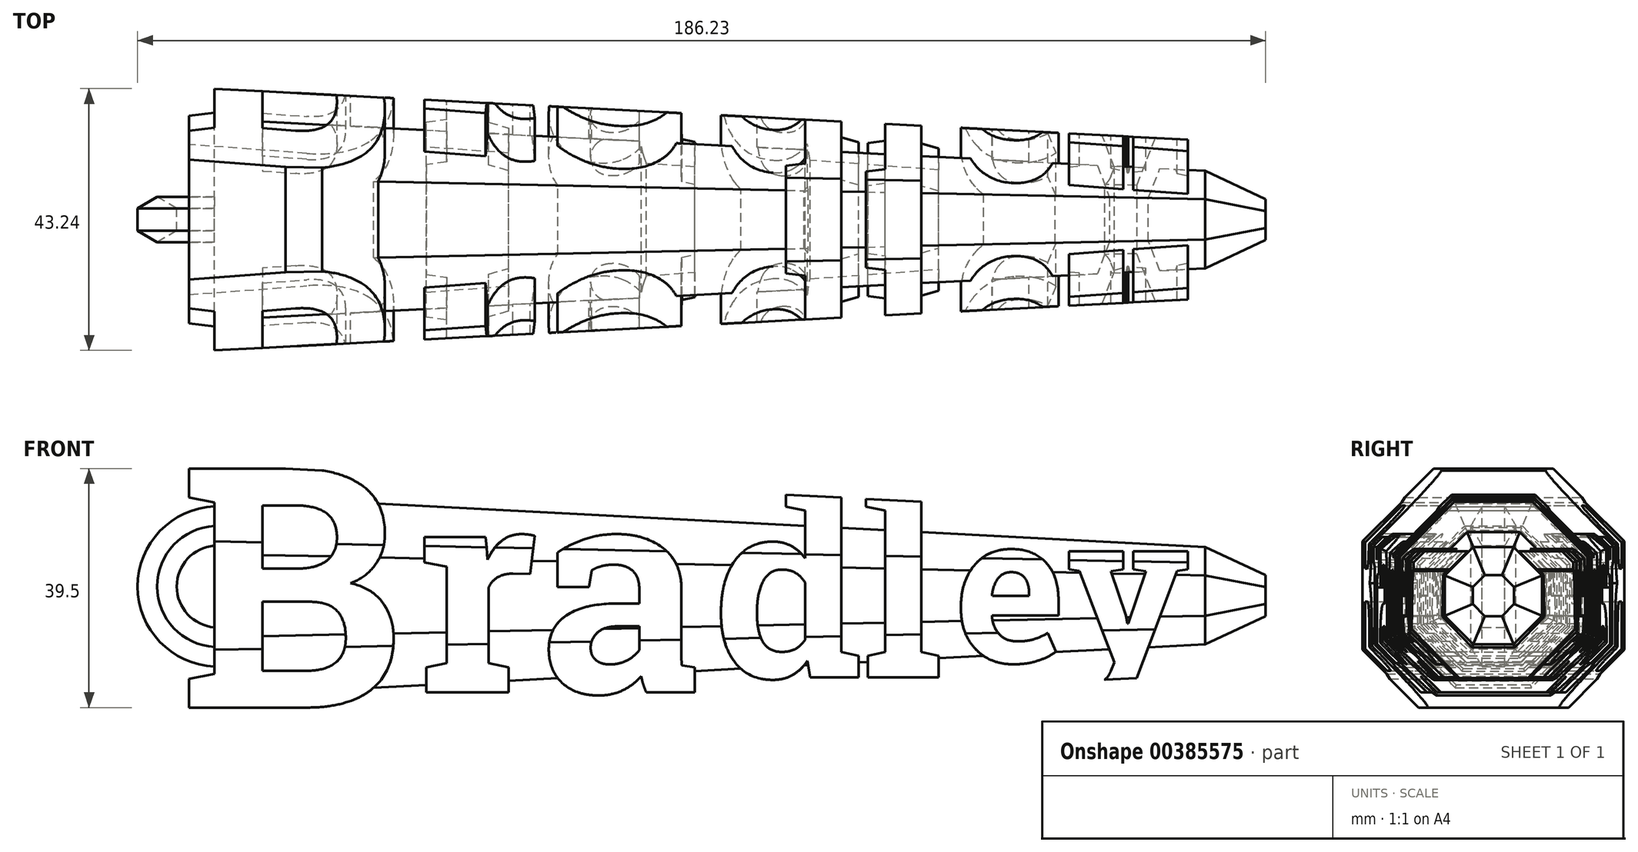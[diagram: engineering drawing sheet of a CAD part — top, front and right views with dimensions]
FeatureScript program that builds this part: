
annotation { "Feature Type Name" : "Feature", "Feature Type Description" : "" }
export const myFeature = defineFeature(function(context is Context, id is Id, definition is map)
    precondition{}
    {
        {
            assignVariable(context, id + "F0", {"name" : "hookPlane", "anyValue" : 78});
        }
        {
            var Q0;
            Q0=qCreatedBy(makeId("Front.planeOp"),FACE);
            var sketch = newSketch(context, id + "F1", { "sketchPlane" : qUnion([Q0])});
            skText(sketch, "E0", { "text": "B", "fontName": "RobotoSlab-Bold.ttf"});
            skPoint(sketch, "E1", {"position": v(-45.56, 0) * mm});
            skText(sketch, "E2", { "text": "ra", "fontName": "RobotoSlab-Bold.ttf"});
            skText(sketch, "E3", { "text": "dl", "fontName": "RobotoSlab-Bold.ttf"});
            skText(sketch, "E4", { "text": "ey", "fontName": "RobotoSlab-Bold.ttf"});
            skPoint(sketch, "E5", {"position": v(3.73, 0) * mm});
            skPoint(sketch, "E6", {"position": v(43.58, 0) * mm});
            skLineSegment(sketch, "E7", {"start": v(-84.26, -20) * mm, "end": v(-84.26, -51.65) * mm, "construction": true});
            skLineSegment(sketch, "E8", {"start": v(-84.26, -51.65) * mm, "end": v(84.26, -51.65) * mm, "construction": true});
            skLineSegment(sketch, "E9", {"start": v(84.26, -51.65) * mm, "end": v(84.26, -12.5) * mm, "construction": true});
            skPoint(sketch, "E10", {"position": v(0, -51.65) * mm});
            const initialGuessF1  = {"E0": [-0.08426, -0.02, 1, 0, 0.04], "E2": [-0.04556, -0.0175, 1, 0, 0.035], "E3": [0.00373, -0.015, 1, 0, 0.03], "E4": [0.04358, -0.0125, 1, 0, 0.025]};
            skSetInitialGuess(sketch, initialGuessF1);
            skSolve(sketch);
        }
        {
            var Q0;
            Q0=qSketchRegion(id+"F1",true);
            extrude(context, id + "F2", {"entities" : qUnion([Q0]), "depth" : 25 * mm, "hasSecondDirection" : true, "secondDirectionOppositeDirection" : true, "secondDirectionDepth" : 25 * mm});
        }
        {
            var Q0;
            Q0=qCreatedBy(makeId("Right.planeOp"),FACE);
            var sketch = newSketch(context, id + "F3", { "sketchPlane" : qUnion([Q0])});
            skCircle(sketch, "E11", {"center": v(0, -1.5) * mm, "radius": 12.5 * mm, "construction": true});
            skLineSegment(sketch, "E12", {"start": v(0, 19.5) * mm, "end": v(0, -20) * mm, "construction": true});
            skLineSegment(sketch, "E13.0", {"start": v(-5.18, 11) * mm, "end": v(5.18, 11) * mm});
            skLineSegment(sketch, "E13.1", {"start": v(5.18, 11) * mm, "end": v(12.5, 3.67) * mm});
            skLineSegment(sketch, "E13.2", {"start": v(12.5, 3.67) * mm, "end": v(12.5, -6.68) * mm});
            skLineSegment(sketch, "E13.3", {"start": v(12.5, -6.68) * mm, "end": v(5.18, -14) * mm});
            skLineSegment(sketch, "E13.4", {"start": v(5.18, -14) * mm, "end": v(-5.18, -14) * mm});
            skLineSegment(sketch, "E13.5", {"start": v(-5.18, -14) * mm, "end": v(-12.5, -6.68) * mm});
            skLineSegment(sketch, "E13.6", {"start": v(-12.5, -6.68) * mm, "end": v(-12.5, 3.67) * mm});
            skLineSegment(sketch, "E13.7", {"start": v(-12.5, 3.67) * mm, "end": v(-5.18, 11) * mm});
            skPoint(sketch, "E13.0.midPoint", {"position": v(0, 11) * mm});
            skSolve(sketch);
        }
        {
            var Q0;
            Q0=qSketchRegion(id+"F3",true);
            var Q1;
            Q1=makeQuery(id+"F2.opExtrude","SWEPT_FACE",FACE,{"disambiguationData":[OSD([sQuery(id+"F1.wireOp",EDGE,"E4.sketch_text.stroke-1")])]});
            extrude(context, id + "F4", {"entities" : qUnion([Q0]), "operationType" : NewBodyOperationType.ADD, "oppositeDirection" : true, "depth" : 78 * mm, "hasDraft" : true, "draftAngle" : 3 * degree, "hasSecondDirection" : true, "secondDirectionOppositeDirection" : false, "secondDirectionBoundEntityFace" : qUnion([Q1]), "secondDirectionDepth" : 85 * mm, "hasSecondDirectionDraft" : true, "secondDirectionDraftAngle" : 3 * degree, "secondDirectionDraftPullDirection" : true});
        }
        {
            var Q0;
            Q0=qCreatedBy(makeId("Right.planeOp"),FACE);
            var sketch = newSketch(context, id + "F5", { "sketchPlane" : qUnion([Q0])});
            skCircle(sketch, "E14.cCircle", {"center": v(0, -1.5) * mm, "radius": 17.5 * mm, "construction": true});
            skLineSegment(sketch, "E14.0", {"start": v(-7.25, 16) * mm, "end": v(7.25, 16) * mm});
            skLineSegment(sketch, "E14.1", {"start": v(7.25, 16) * mm, "end": v(17.5, 5.75) * mm});
            skLineSegment(sketch, "E14.2", {"start": v(17.5, 5.75) * mm, "end": v(17.5, -8.75) * mm});
            skLineSegment(sketch, "E14.3", {"start": v(17.5, -8.75) * mm, "end": v(7.25, -19) * mm});
            skLineSegment(sketch, "E14.4", {"start": v(7.25, -19) * mm, "end": v(-7.25, -19) * mm});
            skLineSegment(sketch, "E14.5", {"start": v(-7.25, -19) * mm, "end": v(-17.5, -8.75) * mm});
            skLineSegment(sketch, "E14.6", {"start": v(-17.5, -8.75) * mm, "end": v(-17.5, 5.75) * mm});
            skLineSegment(sketch, "E14.7", {"start": v(-17.5, 5.75) * mm, "end": v(-7.25, 16) * mm});
            skPoint(sketch, "E14.0.midPoint", {"position": v(0, 16) * mm});
            skLineSegment(sketch, "E15.bottom", {"start": v(40.52, 36.35) * mm, "end": v(-40.52, 36.35) * mm});
            skLineSegment(sketch, "E15.top", {"start": v(40.52, -39.36) * mm, "end": v(-40.52, -39.36) * mm});
            skLineSegment(sketch, "E15.left", {"start": v(40.52, 36.35) * mm, "end": v(40.52, -39.36) * mm});
            skLineSegment(sketch, "E15.right", {"start": v(-40.52, 36.35) * mm, "end": v(-40.52, -39.36) * mm});
            skLineSegment(sketch, "E16", {"start": v(0, 19.5) * mm, "end": v(0, -20) * mm, "construction": true});
            skSolve(sketch);
        }
        {
            var Q0;
            Q0=makeQuery(id+"F5.imprint","IMPRINT",FACE,{"disambiguationData":[TD([[makeQuery(id+"F5.imprint","IMPRINT",EDGE,{"derivedFrom":sQuery(id+"F5.wireOp",EDGE,"E14.0")}),1.0]])]});
            extrude(context, id + "F6", {"entities" : qUnion([Q0]), "operationType" : NewBodyOperationType.REMOVE, "endBound" : BoundingType.THROUGH_ALL, "depth" : 25 * mm, "hasDraft" : true, "draftAngle" : 3 * degree, "hasSecondDirection" : true, "secondDirectionBound" : SecondDirectionBoundingType.THROUGH_ALL, "secondDirectionOppositeDirection" : true, "secondDirectionDepth" : 25 * mm, "hasSecondDirectionDraft" : true, "secondDirectionDraftAngle" : 3 * degree, "secondDirectionDraftPullDirection" : true});
        }
        {
            var Q0;
            {var subQ0=sQuery(id+"F3.wireOp",EDGE,"E13.3");var subQ1=sQuery(id+"F3.wireOp",EDGE,"E13.2");var subQ2=sQuery(id+"F3.wireOp",EDGE,"E13.4");var subQ3=sQuery(id+"F3.wireOp",EDGE,"E13.5");var subQ4=sQuery(id+"F3.wireOp",EDGE,"E13.6");Q0=makeQuery(id+"F4.boolean.opBoolean","SPLIT",FACE,{"disambiguationData":[TD([makeQuery(id+"F2.opExtrude","SWEPT_FACE",FACE,{"disambiguationData":[OSD([sQuery(id+"F1.wireOp",EDGE,"E4.sketch_text.stroke-0")])]})])],"derivedFrom":makeQuery(id+"F4.opExtrude","CAP_FACE",FACE,{"disambiguationData":[OSD([sQuery(id+"F3.wireOp",EDGE,"E13.0"),sQuery(id+"F3.wireOp",EDGE,"E13.1"),subQ1,subQ0,subQ2,subQ3,subQ4,sQuery(id+"F3.wireOp",EDGE,"E13.7")])],"isStart":true})});}
            var sketch = newSketch(context, id + "F7", { "sketchPlane" : qUnion([Q0])});
            skCircle(sketch, "E17.cCircle", {"center": v(0, -1.5) * mm, "radius": 8.05 * mm, "construction": true});
            skLineSegment(sketch, "E17.0", {"start": v(-3.33, 6.54) * mm, "end": v(3.33, 6.54) * mm});
            skLineSegment(sketch, "E17.1", {"start": v(3.33, 6.54) * mm, "end": v(8.05, 1.83) * mm});
            skLineSegment(sketch, "E17.2", {"start": v(8.05, 1.83) * mm, "end": v(8.05, -4.84) * mm});
            skLineSegment(sketch, "E17.3", {"start": v(8.05, -4.84) * mm, "end": v(3.33, -9.55) * mm});
            skLineSegment(sketch, "E17.4", {"start": v(3.33, -9.55) * mm, "end": v(-3.33, -9.55) * mm});
            skLineSegment(sketch, "E17.5", {"start": v(-3.33, -9.55) * mm, "end": v(-8.05, -4.84) * mm});
            skLineSegment(sketch, "E17.6", {"start": v(-8.05, -4.84) * mm, "end": v(-8.05, 1.83) * mm});
            skLineSegment(sketch, "E17.7", {"start": v(-8.05, 1.83) * mm, "end": v(-3.33, 6.54) * mm});
            skPoint(sketch, "E17.0.midPoint", {"position": v(0, 6.54) * mm});
            skLineSegment(sketch, "E18", {"start": v(0, 19.59) * mm, "end": v(0, -20.57) * mm, "construction": true});
            skSolve(sketch);
        }
        {
            var Q0;
            Q0=qSketchRegion(id+"F7",true);
            extrude(context, id + "F8", {"entities" : qUnion([Q0]), "operationType" : NewBodyOperationType.ADD, "depth" : 10 * mm, "hasDraft" : true, "draftAngle" : 25 * degree, "draftPullDirection" : true});
        }
        {
            var Q0;
            Q0=qCreatedBy(makeId("Right.planeOp"),FACE);
            cPlane(context, id + "F9", {"entities" : qUnion([Q0]), "cplaneType" : CPlaneType.OFFSET, "offset" : (getVariable(context, 'hookPlane')) * mm, "oppositeDirection" : true, "width" : 150 * mm, "height" : 150 * mm});
        }
        {
            var Q0;
            Q0=qCreatedBy(makeId("Front.planeOp"),FACE);
            var sketch = newSketch(context, id + "F10", { "sketchPlane" : qUnion([Q0])});
            skArc(sketch, "E19", {"start": v(-73, 8.66) * mm, "mid": v(-88, 0) * mm, "end": v(-73, -8.66) * mm});
            skSolve(sketch);
        }
        {
            var Q0;
            Q0=qCreatedBy(id+"F9.planeOp",FACE);
            var sketch = newSketch(context, id + "F11", { "sketchPlane" : qUnion([Q0])});
            skCircle(sketch, "E20.cCircle", {"center": v(0, 10) * mm, "radius": 3.23 * mm, "construction": true});
            skLineSegment(sketch, "E20.0", {"start": v(1.87, 6.77) * mm, "end": v(-1.87, 6.77) * mm});
            skLineSegment(sketch, "E20.1", {"start": v(-1.87, 6.77) * mm, "end": v(-3.73, 10) * mm});
            skLineSegment(sketch, "E20.2", {"start": v(-3.73, 10) * mm, "end": v(-1.87, 13.23) * mm});
            skLineSegment(sketch, "E20.3", {"start": v(-1.87, 13.23) * mm, "end": v(1.87, 13.23) * mm});
            skLineSegment(sketch, "E20.4", {"start": v(1.87, 13.23) * mm, "end": v(3.73, 10) * mm});
            skLineSegment(sketch, "E20.5", {"start": v(3.73, 10) * mm, "end": v(1.87, 6.77) * mm});
            skPoint(sketch, "E20.0.midPoint", {"position": v(0, 6.77) * mm});
            skSolve(sketch);
        }
        {
            var Q0;
            Q0=qSketchRegion(id+"F11",true);
            var Q1;
            Q1=qConstructionFilter(qBodyType(qCreatedBy(id+"F10",EDGE),BodyType.WIRE),ConstructionObject.NO);
            sweep(context, id + "F12", {"operationType" : NewBodyOperationType.ADD, "profiles" : qUnion([Q0]), "path" : qUnion([Q1])});
        }
    });
